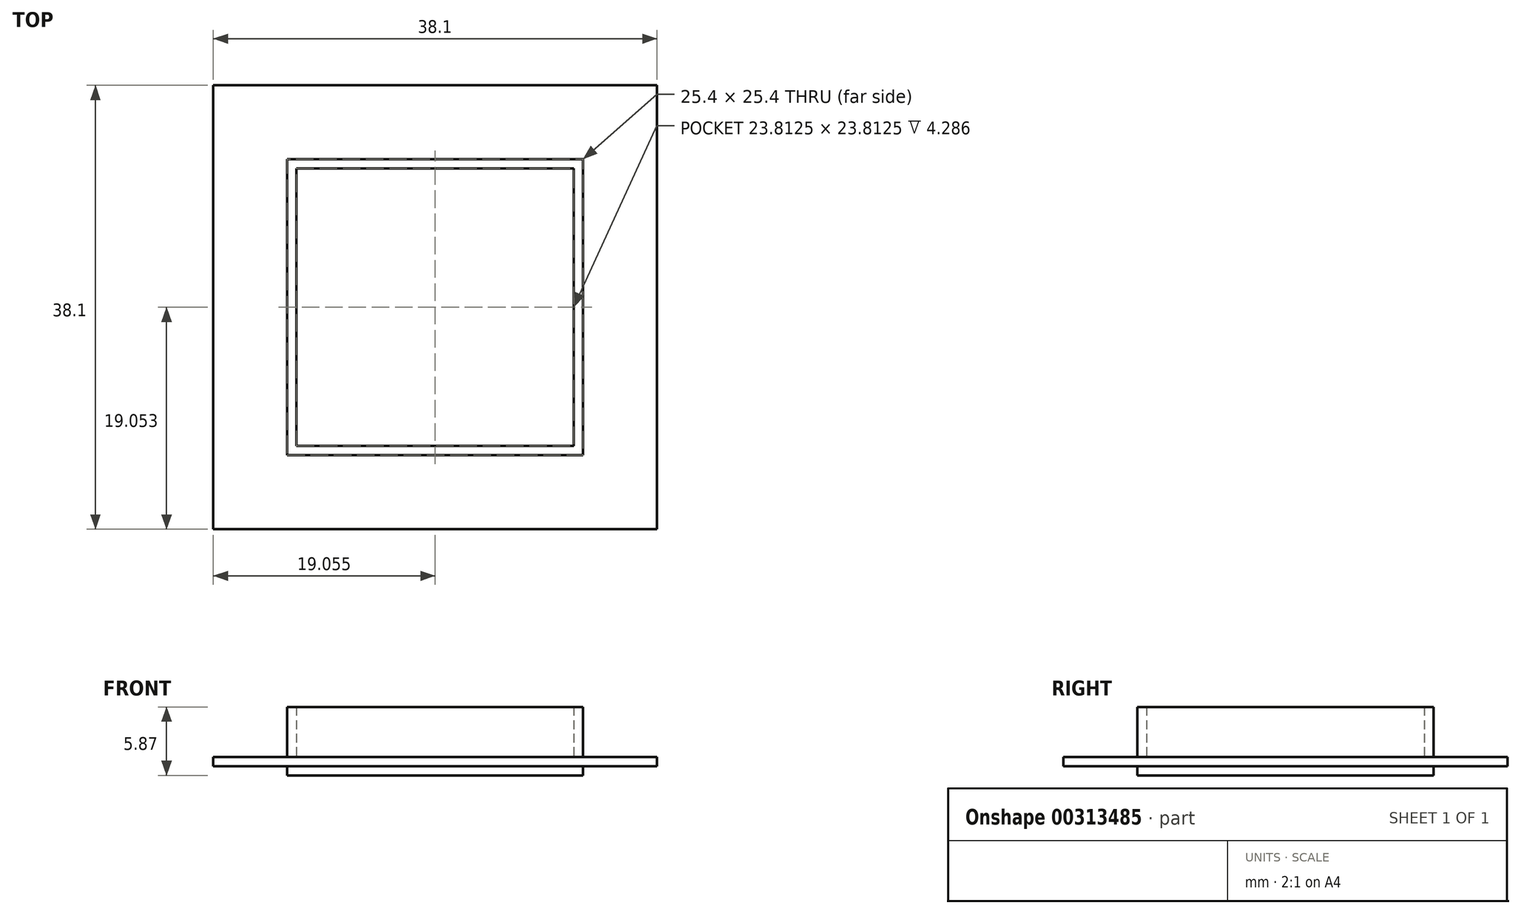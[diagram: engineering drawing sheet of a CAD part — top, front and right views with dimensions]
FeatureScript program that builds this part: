
annotation { "Feature Type Name" : "Feature", "Feature Type Description" : "" }
export const myFeature = defineFeature(function(context is Context, id is Id, definition is map)
    precondition{}
    {
        {
            var Q0;
            Q0=qCreatedBy(makeId("Top.planeOp"),FACE);
            var sketch = newSketch(context, id + "F0", { "sketchPlane" : qUnion([Q0])});
            skLineSegment(sketch, "E0.bottom", {"start": v(18.76, 24.76) * mm, "end": v(-19.34, 24.76) * mm});
            skLineSegment(sketch, "E0.top", {"start": v(18.76, -13.34) * mm, "end": v(-19.34, -13.34) * mm});
            skLineSegment(sketch, "E0.left", {"start": v(18.76, 24.76) * mm, "end": v(18.76, -13.34) * mm});
            skLineSegment(sketch, "E0.right", {"start": v(-19.34, 24.76) * mm, "end": v(-19.34, -13.34) * mm});
            skSolve(sketch);
        }
        {
            var Q0;
            Q0=makeQuery(id+"F0.imprint","IMPRINT",FACE,{"disambiguationData":[TD([[makeQuery(id+"F0.imprint","IMPRINT",EDGE,{"derivedFrom":sQuery(id+"F0.wireOp",EDGE,"E0.bottom")}),1.0]])]});
            extrude(context, id + "F1", {"entities" : qUnion([Q0]), "depth" : 0.8 * mm});
        }
        {
            var Q0;
            Q0=qCreatedBy(makeId("Top.planeOp"),FACE);
            var sketch = newSketch(context, id + "F2", { "sketchPlane" : qUnion([Q0])});
            skLineSegment(sketch, "E1.0", {"start": v(18.76, 24.09) * mm, "end": v(-19.34, 24.09) * mm});
            skLineSegment(sketch, "E2.0", {"start": v(-12.99, -6.99) * mm, "end": v(12.41, -6.99) * mm});
            skLineSegment(sketch, "E2.1", {"start": v(-12.99, 18.41) * mm, "end": v(-12.99, -6.99) * mm});
            skLineSegment(sketch, "E2.2", {"start": v(12.41, 18.41) * mm, "end": v(-12.99, 18.41) * mm});
            skLineSegment(sketch, "E2.3", {"start": v(12.41, -6.99) * mm, "end": v(12.41, 18.41) * mm});
            skSolve(sketch);
        }
        {
            var Q0;
            Q0=makeQuery(id+"F2.imprint","IMPRINT",FACE,{"disambiguationData":[TD([[makeQuery(id+"F2.imprint","IMPRINT",EDGE,{"derivedFrom":sQuery(id+"F2.wireOp",EDGE,"E2.0")}),1.0]])]});
            var sketch = newSketch(context, id + "F3", { "sketchPlane" : qUnion([Q0])});
            skSolve(sketch);
        }
        {
            var Q0;
            Q0=makeQuery(id+"F2.imprint","IMPRINT",FACE,{"disambiguationData":[TD([[makeQuery(id+"F2.imprint","IMPRINT",EDGE,{"derivedFrom":sQuery(id+"F2.wireOp",EDGE,"E2.0")}),1.0]])]});
            extrude(context, id + "F4", {"entities" : qUnion([Q0]), "oppositeDirection" : true, "depth" : 0.8 * mm});
        }
        {
            var Q0;
            Q0=makeQuery(id+"F3.imprint","IMPRINT",FACE,{"disambiguationData":[TD([[makeQuery(id+"F3.imprint","IMPRINT",EDGE,{"derivedFrom":makeQuery(id+"F2.imprint","IMPRINT",EDGE,{"derivedFrom":sQuery(id+"F2.wireOp",EDGE,"E2.0")})}),1.0]])]});
            var sketch = newSketch(context, id + "F5", { "sketchPlane" : qUnion([Q0])});
            skLineSegment(sketch, "E3.0", {"start": v(11.62, 17.62) * mm, "end": v(-12.2, 17.62) * mm});
            skLineSegment(sketch, "E3.1", {"start": v(11.62, -6.2) * mm, "end": v(11.62, 17.62) * mm});
            skLineSegment(sketch, "E3.2", {"start": v(-12.2, -6.2) * mm, "end": v(11.62, -6.2) * mm});
            skLineSegment(sketch, "E3.3", {"start": v(-12.2, 17.62) * mm, "end": v(-12.2, -6.2) * mm});
            skSolve(sketch);
        }
        {
            var Q0;
            Q0=makeQuery(id+"F5.imprint","IMPRINT",FACE,{"disambiguationData":[TD([[makeQuery(id+"F5.imprint","IMPRINT",EDGE,{"derivedFrom":sQuery(id+"F5.wireOp",EDGE,"E3.0")}),-1.0]])]});
            extrude(context, id + "F6", {"entities" : qUnion([Q0]), "operationType" : NewBodyOperationType.ADD, "depth" : 5.08 * mm});
        }
    });
